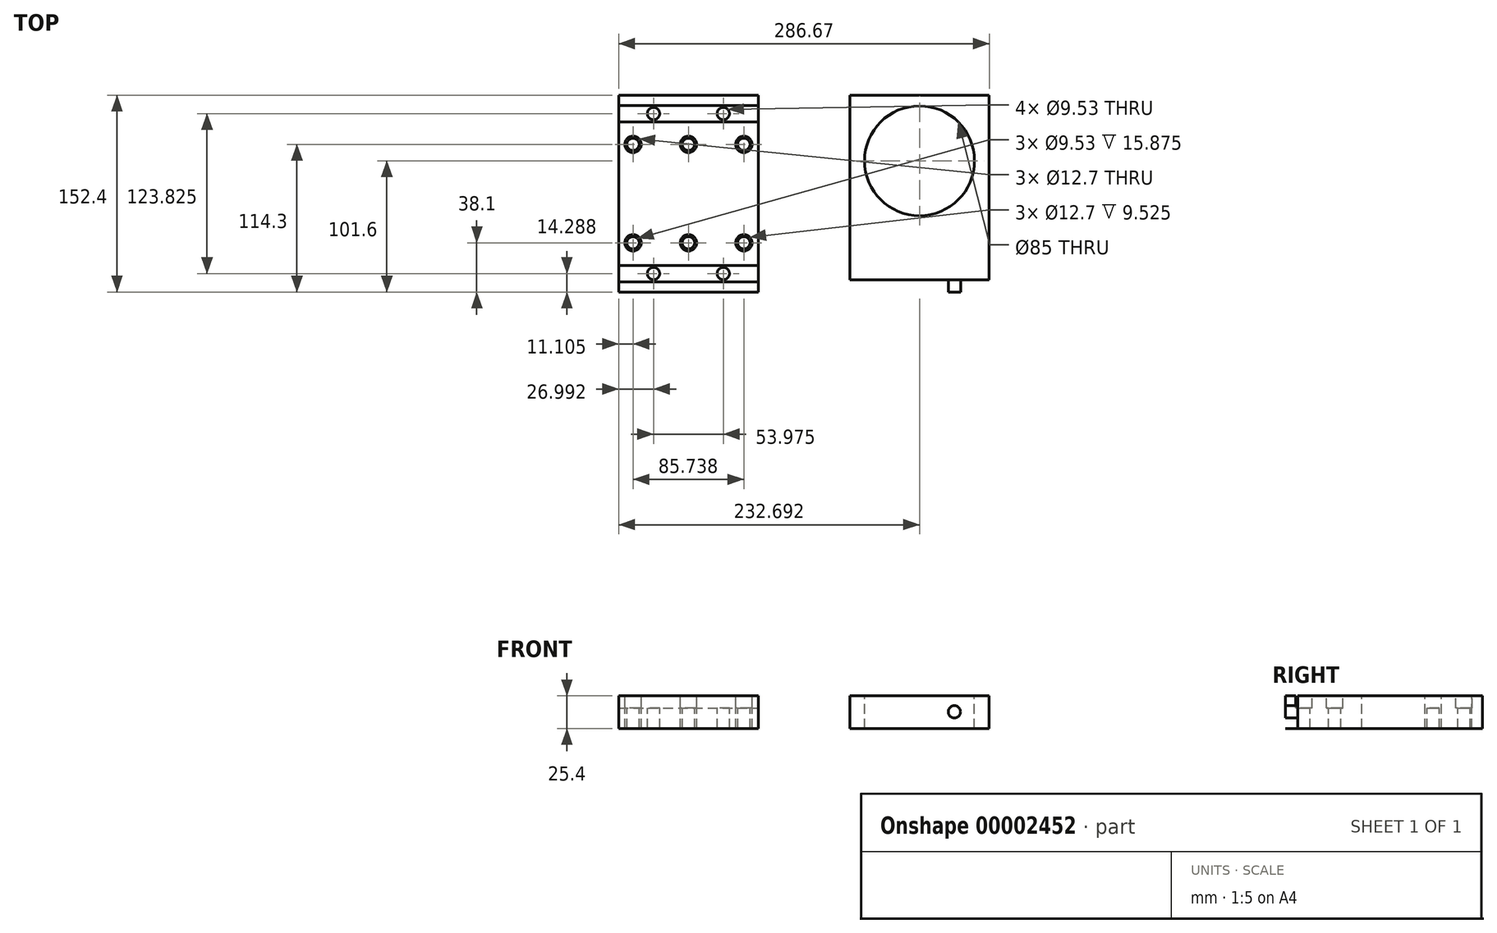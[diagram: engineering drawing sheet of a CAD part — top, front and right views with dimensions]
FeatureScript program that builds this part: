
annotation { "Feature Type Name" : "Feature", "Feature Type Description" : "" }
export const myFeature = defineFeature(function(context is Context, id is Id, definition is map)
    precondition{}
    {
        {
            var Q0;
            Q0=qCreatedBy(makeId("Top.planeOp"),FACE);
            var sketch = newSketch(context, id + "F0", { "sketchPlane" : qUnion([Q0])});
            skCircle(sketch, "E0", {"center": v(42.86, -38.1) * mm, "radius": 4.76 * mm});
            skCircle(sketch, "E1", {"center": v(0, -38.1) * mm, "radius": 4.76 * mm});
            skCircle(sketch, "E2", {"center": v(-42.88, -38.1) * mm, "radius": 4.76 * mm});
            skLineSegment(sketch, "E3", {"start": v(0, 0) * mm, "end": v(50.87, 0) * mm, "construction": true});
            skCircle(sketch, "E4.0.MirrorC", {"center": v(42.86, 38.1) * mm, "radius": 4.76 * mm});
            skCircle(sketch, "E5.0.MirrorC", {"center": v(0, 38.1) * mm, "radius": 4.76 * mm});
            skCircle(sketch, "E6.0.MirrorC", {"center": v(-42.88, 38.1) * mm, "radius": 4.76 * mm});
            skLineSegment(sketch, "E7.rect.bottom", {"start": v(-53.97, 76.2) * mm, "end": v(53.98, 76.2) * mm});
            skLineSegment(sketch, "E7.rect.top", {"start": v(-53.98, -76.2) * mm, "end": v(53.97, -76.2) * mm});
            skLineSegment(sketch, "E7.rect.left", {"start": v(-53.97, 76.2) * mm, "end": v(-53.98, -76.2) * mm});
            skLineSegment(sketch, "E7.rect.right", {"start": v(53.98, 76.2) * mm, "end": v(53.97, -76.2) * mm});
            skPoint(sketch, "E7.rect.middle", {"position": v(0, 0) * mm});
            skLineSegment(sketch, "E8.rect.bottom", {"start": v(-53.98, 68.26) * mm, "end": v(53.98, 68.26) * mm});
            skLineSegment(sketch, "E8.rect.top", {"start": v(-53.98, 55.56) * mm, "end": v(53.98, 55.56) * mm});
            skLineSegment(sketch, "E8.rect.left", {"start": v(-53.97, 68.26) * mm, "end": v(-53.97, 55.56) * mm});
            skLineSegment(sketch, "E8.rect.right", {"start": v(53.97, 68.26) * mm, "end": v(53.97, 55.56) * mm});
            skPoint(sketch, "E8.rect.middle", {"position": v(0, 61.91) * mm});
            skLineSegment(sketch, "E9.rect.bottom", {"start": v(-53.98, -55.56) * mm, "end": v(53.98, -55.56) * mm});
            skLineSegment(sketch, "E9.rect.top", {"start": v(-53.98, -68.26) * mm, "end": v(53.98, -68.26) * mm});
            skLineSegment(sketch, "E9.rect.left", {"start": v(-53.98, -55.56) * mm, "end": v(-53.98, -68.26) * mm});
            skLineSegment(sketch, "E9.rect.right", {"start": v(53.98, -55.56) * mm, "end": v(53.98, -68.26) * mm});
            skPoint(sketch, "E9.rect.middle", {"position": v(0, -61.91) * mm});
            skLineSegment(sketch, "E10", {"start": v(-53.98, -47.62) * mm, "end": v(53.98, -47.63) * mm, "construction": true});
            skCircle(sketch, "E11", {"center": v(-26.99, -61.91) * mm, "radius": 4.76 * mm});
            skCircle(sketch, "E12", {"center": v(26.99, -61.91) * mm, "radius": 4.76 * mm});
            skCircle(sketch, "E13.0.MirrorC", {"center": v(26.99, 61.91) * mm, "radius": 4.76 * mm});
            skCircle(sketch, "E14.0.MirrorC", {"center": v(-26.99, 61.91) * mm, "radius": 4.76 * mm});
            skCircle(sketch, "E15", {"center": v(-42.88, 38.1) * mm, "radius": 6.35 * mm});
            skCircle(sketch, "E16", {"center": v(42.86, 38.1) * mm, "radius": 6.35 * mm});
            skCircle(sketch, "E17", {"center": v(0, 38.1) * mm, "radius": 6.35 * mm});
            skCircle(sketch, "E18", {"center": v(-42.88, -38.1) * mm, "radius": 6.35 * mm});
            skCircle(sketch, "E19", {"center": v(0, -38.1) * mm, "radius": 6.35 * mm});
            skCircle(sketch, "E20", {"center": v(42.86, -38.1) * mm, "radius": 6.35 * mm});
            skLineSegment(sketch, "E21.rect.bottom", {"start": v(124.74, 76.2) * mm, "end": v(232.69, 76.2) * mm});
            skLineSegment(sketch, "E21.rect.top", {"start": v(124.74, -76.2) * mm, "end": v(232.69, -76.2) * mm});
            skLineSegment(sketch, "E21.rect.left", {"start": v(124.74, 76.2) * mm, "end": v(124.74, -76.2) * mm});
            skLineSegment(sketch, "E21.rect.right", {"start": v(232.69, 76.2) * mm, "end": v(232.69, -76.2) * mm});
            skPoint(sketch, "E21.rect.middle", {"position": v(178.71, 0) * mm});
            skCircle(sketch, "E22", {"center": v(178.71, 25.4) * mm, "radius": 42.5 * mm});
            skSolve(sketch);
        }
        {
            var Q0;
            {var subQ0=sQuery(id+"F0.wireOp",EDGE,"E8.rect.bottom");var subQ1=makeQuery(id+"F0.imprint","IMPRINT",EDGE,{"derivedFrom":subQ0});var subQ4=sQuery(id+"F0.wireOp",EDGE,"E7.rect.bottom");var subQ10=sQuery(id+"F0.wireOp",EDGE,"E7.rect.top");var subQ12=sQuery(id+"F0.wireOp",EDGE,"E8.rect.top");var subQ13=makeQuery(id+"F0.imprint","IMPRINT",EDGE,{"derivedFrom":subQ12});var subQ14=sQuery(id+"F0.wireOp",EDGE,"E9.rect.bottom");var subQ15=makeQuery(id+"F0.imprint","IMPRINT",EDGE,{"derivedFrom":subQ14});Q0=qUnion([makeQuery(id+"F0.imprint","IMPRINT",FACE,{"disambiguationData":[TD([[makeQuery(id+"F0.imprint","IMPRINT",EDGE,{"derivedFrom":subQ4}),-1.0]])]}),makeQuery(id+"F0.imprint","IMPRINT",FACE,{"disambiguationData":[TD([[makeQuery(id+"F0.imprint","IMPRINT",EDGE,{"derivedFrom":subQ10}),1.0]])]}),makeQuery(id+"F0.imprint","IMPRINT",FACE,{"disambiguationData":[TD([[subQ1,-1.0]])]}),makeQuery(id+"F0.imprint","IMPRINT",FACE,{"disambiguationData":[TD([[subQ15,-1.0]])]}),makeQuery(id+"F0.imprint","IMPRINT",FACE,{"disambiguationData":[TD([[subQ13,-1.0]])]}),makeQuery(id+"F0.imprint","IMPRINT",FACE,{"disambiguationData":[TD([[makeQuery(id+"F0.imprint","IMPRINT",EDGE,{"derivedFrom":sQuery(id+"F0.wireOp",EDGE,"E21.rect.bottom")}),-1.0]])]})]);}
            var Q1;
            Q1=makeQuery(id+"F0.imprint","IMPRINT",FACE,{"disambiguationData":[TD([[makeQuery(id+"F0.imprint","IMPRINT",EDGE,{"derivedFrom":sQuery(id+"F0.wireOp",EDGE,"E6.0.MirrorC")}),1.0]])]});
            var Q2;
            Q2=makeQuery(id+"F0.imprint","IMPRINT",FACE,{"disambiguationData":[TD([[makeQuery(id+"F0.imprint","IMPRINT",EDGE,{"derivedFrom":sQuery(id+"F0.wireOp",EDGE,"E5.0.MirrorC")}),1.0]])]});
            var Q3;
            Q3=makeQuery(id+"F0.imprint","IMPRINT",FACE,{"disambiguationData":[TD([[makeQuery(id+"F0.imprint","IMPRINT",EDGE,{"derivedFrom":sQuery(id+"F0.wireOp",EDGE,"E4.0.MirrorC")}),1.0]])]});
            var Q4;
            Q4=makeQuery(id+"F0.imprint","IMPRINT",FACE,{"disambiguationData":[TD([[makeQuery(id+"F0.imprint","IMPRINT",EDGE,{"derivedFrom":sQuery(id+"F0.wireOp",EDGE,"E2")}),-1.0]])]});
            var Q5;
            Q5=makeQuery(id+"F0.imprint","IMPRINT",FACE,{"disambiguationData":[TD([[makeQuery(id+"F0.imprint","IMPRINT",EDGE,{"derivedFrom":sQuery(id+"F0.wireOp",EDGE,"E1")}),-1.0]])]});
            var Q6;
            Q6=makeQuery(id+"F0.imprint","IMPRINT",FACE,{"disambiguationData":[TD([[makeQuery(id+"F0.imprint","IMPRINT",EDGE,{"derivedFrom":sQuery(id+"F0.wireOp",EDGE,"E0")}),-1.0]])]});
            extrude(context, id + "F1", {"entities" : qUnion([Q0, Q1, Q2, Q3, Q4, Q5, Q6]), "oppositeDirection" : true, "depth" : 25.4 * mm});
        }
        {
            var Q0;
            Q0=makeQuery(id+"F0.imprint","IMPRINT",FACE,{"disambiguationData":[TD([[makeQuery(id+"F0.imprint","IMPRINT",EDGE,{"derivedFrom":sQuery(id+"F0.wireOp",EDGE,"E9.rect.bottom")}),-1.0]])]});
            var Q1;
            Q1=makeQuery(id+"F0.imprint","IMPRINT",FACE,{"disambiguationData":[TD([[makeQuery(id+"F0.imprint","IMPRINT",EDGE,{"derivedFrom":sQuery(id+"F0.wireOp",EDGE,"E8.rect.bottom")}),-1.0]])]});
            var Q2;
            Q2=makeQuery(id+"F0.imprint","IMPRINT",FACE,{"disambiguationData":[TD([[makeQuery(id+"F0.imprint","IMPRINT",EDGE,{"derivedFrom":sQuery(id+"F0.wireOp",EDGE,"E2")}),-1.0]])]});
            var Q3;
            Q3=makeQuery(id+"F0.imprint","IMPRINT",FACE,{"disambiguationData":[TD([[makeQuery(id+"F0.imprint","IMPRINT",EDGE,{"derivedFrom":sQuery(id+"F0.wireOp",EDGE,"E1")}),-1.0]])]});
            var Q4;
            Q4=makeQuery(id+"F0.imprint","IMPRINT",FACE,{"disambiguationData":[TD([[makeQuery(id+"F0.imprint","IMPRINT",EDGE,{"derivedFrom":sQuery(id+"F0.wireOp",EDGE,"E0")}),-1.0]])]});
            var Q5;
            Q5=makeQuery(id+"F0.imprint","IMPRINT",FACE,{"disambiguationData":[TD([[makeQuery(id+"F0.imprint","IMPRINT",EDGE,{"derivedFrom":sQuery(id+"F0.wireOp",EDGE,"E6.0.MirrorC")}),1.0]])]});
            var Q6;
            Q6=makeQuery(id+"F0.imprint","IMPRINT",FACE,{"disambiguationData":[TD([[makeQuery(id+"F0.imprint","IMPRINT",EDGE,{"derivedFrom":sQuery(id+"F0.wireOp",EDGE,"E5.0.MirrorC")}),1.0]])]});
            var Q7;
            Q7=makeQuery(id+"F0.imprint","IMPRINT",FACE,{"disambiguationData":[TD([[makeQuery(id+"F0.imprint","IMPRINT",EDGE,{"derivedFrom":sQuery(id+"F0.wireOp",EDGE,"E4.0.MirrorC")}),1.0]])]});
            extrude(context, id + "F2", {"entities" : qUnion([Q0, Q1, Q2, Q3, Q4, Q5, Q6, Q7]), "operationType" : NewBodyOperationType.REMOVE, "oppositeDirection" : true, "depth" : 9.52 * mm});
        }
        {
            var Q0;
            Q0=makeQuery(id+"F1.opExtrude","SWEPT_FACE",FACE,{"disambiguationData":[OSD([sQuery(id+"F0.wireOp",EDGE,"E21.rect.top")])]});
            var sketch = newSketch(context, id + "F3", { "sketchPlane" : qUnion([Q0])});
            skLineSegment(sketch, "E23", {"start": v(178.71, 0) * mm, "end": v(178.71, -25.4) * mm, "construction": true});
            skLineSegment(sketch, "E24.rect.bottom", {"start": v(124.74, -6.35) * mm, "end": v(232.69, -6.35) * mm});
            skLineSegment(sketch, "E24.rect.top", {"start": v(124.74, -19.05) * mm, "end": v(232.69, -19.05) * mm});
            skLineSegment(sketch, "E24.rect.left", {"start": v(124.74, -6.35) * mm, "end": v(124.74, -19.05) * mm});
            skLineSegment(sketch, "E24.rect.right", {"start": v(232.69, -6.35) * mm, "end": v(232.69, -19.05) * mm});
            skPoint(sketch, "E24.rect.middle", {"position": v(178.71, -12.7) * mm});
            skCircle(sketch, "E25", {"center": v(151.72, -12.4) * mm, "radius": 4.76 * mm});
            skCircle(sketch, "E26.0.MirrorC", {"center": v(205.7, -12.4) * mm, "radius": 4.76 * mm});
            skSolve(sketch);
        }
        {
            var Q0;
            {var subQ2=sQuery(id+"F3.wireOp",EDGE,"E24.rect.bottom");Q0=makeQuery(id+"F3.imprint","IMPRINT",FACE,{"disambiguationData":[TD([[makeQuery(id+"F3.imprint","IMPRINT",EDGE,{"derivedFrom":subQ2}),1.0]])]});}
            var Q1;
            {var subQ2=sQuery(id+"F3.wireOp",EDGE,"E24.rect.top");Q1=makeQuery(id+"F3.imprint","IMPRINT",FACE,{"disambiguationData":[TD([[makeQuery(id+"F3.imprint","IMPRINT",EDGE,{"derivedFrom":subQ2}),-1.0]])]});}
            var Q2;
            Q2=makeQuery(id+"F3.imprint","IMPRINT",FACE,{"disambiguationData":[TD([[makeQuery(id+"F3.imprint","IMPRINT",EDGE,{"derivedFrom":sQuery(id+"F3.wireOp",EDGE,"E25")}),1.0]])]});
            var Q3;
            Q3=makeQuery(id+"F3.imprint","IMPRINT",FACE,{"disambiguationData":[TD([[makeQuery(id+"F3.imprint","IMPRINT",EDGE,{"derivedFrom":sQuery(id+"F3.wireOp",EDGE,"E26.0.MirrorC")}),-1.0]])]});
            extrude(context, id + "F4", {"entities" : qUnion([Q0, Q1, Q2, Q3]), "operationType" : NewBodyOperationType.REMOVE, "oppositeDirection" : true, "depth" : 9.52 * mm});
        }
    });
